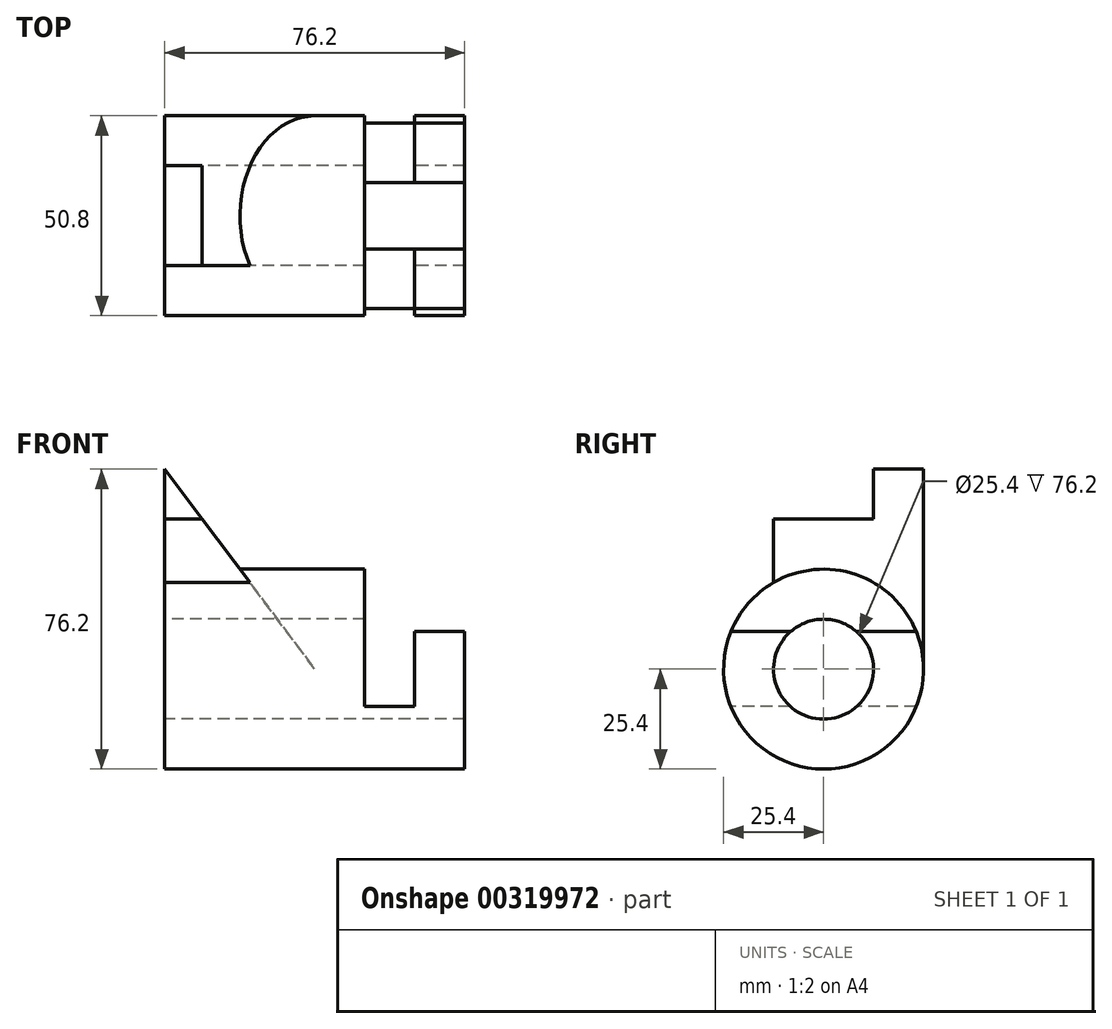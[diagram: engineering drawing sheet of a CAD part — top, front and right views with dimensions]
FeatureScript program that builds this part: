
annotation { "Feature Type Name" : "Feature", "Feature Type Description" : "" }
export const myFeature = defineFeature(function(context is Context, id is Id, definition is map)
    precondition{}
    {
        {
            var Q0;
            Q0=qCreatedBy(makeId("Front.planeOp"),FACE);
            var sketch = newSketch(context, id + "F0", { "sketchPlane" : qUnion([Q0])});
            skLineSegment(sketch, "E0", {"start": v(0, 0) * mm, "end": v(0, 25.4) * mm});
            skLineSegment(sketch, "E1", {"start": v(0, 25.4) * mm, "end": v(76.2, 25.4) * mm});
            skLineSegment(sketch, "E2", {"start": v(76.2, 25.4) * mm, "end": v(76.2, 0) * mm});
            skLineSegment(sketch, "E3", {"start": v(0, 0) * mm, "end": v(76.2, 0) * mm});
            skLineSegment(sketch, "E4", {"start": v(-18.96, 0) * mm, "end": v(97.99, 0) * mm, "construction": true});
            skSolve(sketch);
        }
        {
            var Q0;
            Q0=makeQuery(id+"F0.imprint","IMPRINT",FACE,{"disambiguationData":[TD([[makeQuery(id+"F0.imprint","IMPRINT",EDGE,{"derivedFrom":sQuery(id+"F0.wireOp",EDGE,"E0")}),-1.0]])]});
            var Q1;
            Q1=sQuery(id+"F0.wireOp",EDGE,"E4");
            revolve(context, id + "F1", {"entities" : qUnion([Q0]), "axis" : qUnion([Q1]), "revolveType" : RevolveType.FULL});
        }
        {
            var Q0;
            Q0=qCreatedBy(makeId("Front.planeOp"),FACE);
            var sketch = newSketch(context, id + "F2", { "sketchPlane" : qUnion([Q0])});
            skLineSegment(sketch, "E5", {"start": v(0, 25.4) * mm, "end": v(76.2, 25.4) * mm});
            skLineSegment(sketch, "E6", {"start": v(76.2, -25.4) * mm, "end": v(0, -25.4) * mm});
            skLineSegment(sketch, "E7.0", {"start": v(76.2, -25.4) * mm, "end": v(76.2, 25.4) * mm});
            skLineSegment(sketch, "E8", {"start": v(50.8, 25.4) * mm, "end": v(50.8, -9.53) * mm});
            skLineSegment(sketch, "E9", {"start": v(50.8, -9.53) * mm, "end": v(63.5, -9.53) * mm});
            skLineSegment(sketch, "E10", {"start": v(63.5, -9.53) * mm, "end": v(63.5, 9.52) * mm});
            skLineSegment(sketch, "E11", {"start": v(63.5, 9.52) * mm, "end": v(76.2, 9.52) * mm});
            skLineSegment(sketch, "E12", {"start": v(50.8, 25.4) * mm, "end": v(76.2, 25.4) * mm});
            skSolve(sketch);
        }
        {
            var Q0;
            Q0 = qSketchRegion(id + "F2", true);
            extrude(context, id + "F3", {"entities" : qUnion([Q0]), "operationType" : NewBodyOperationType.REMOVE, "endBound" : BoundingType.THROUGH_ALL, "oppositeDirection" : true, "depth" : 25.4 * mm, "hasSecondDirection" : true, "secondDirectionBound" : SecondDirectionBoundingType.THROUGH_ALL, "secondDirectionOppositeDirection" : false, "secondDirectionDepth" : 25.4 * mm});
        }
        {
            var Q0;
            Q0=qCreatedBy(makeId("Right.planeOp"),FACE);
            var sketch = newSketch(context, id + "F4", { "sketchPlane" : qUnion([Q0])});
            skArc(sketch, "E13.0", {"start": v(23.55, -9.53) * mm, "mid": v(0, 25.4) * mm, "end": v(-23.55, -9.53) * mm});
            skLineSegment(sketch, "E14", {"start": v(-12.7, 22) * mm, "end": v(-12.7, 38.1) * mm});
            skLineSegment(sketch, "E15", {"start": v(-12.7, 38.1) * mm, "end": v(12.7, 38.1) * mm});
            skLineSegment(sketch, "E16", {"start": v(12.7, 38.1) * mm, "end": v(12.7, 50.8) * mm});
            skLineSegment(sketch, "E17", {"start": v(12.7, 50.8) * mm, "end": v(25.4, 50.8) * mm});
            skLineSegment(sketch, "E18", {"start": v(25.4, 50.8) * mm, "end": v(25.4, 0) * mm});
            skSolve(sketch);
        }
        {
            var Q0;
            {var subQ0=sQuery(id+"F4.wireOp",EDGE,"E14");Q0=makeQuery(id+"F4.imprint","IMPRINT",FACE,{"disambiguationData":[TD([[makeQuery(id+"F4.imprint","IMPRINT",EDGE,{"derivedFrom":subQ0}),-1.0]])]});}
            extrude(context, id + "F5", {"entities" : qUnion([Q0]), "operationType" : NewBodyOperationType.ADD, "depth" : 38.1 * mm});
        }
        {
            var Q0;
            Q0=makeQuery(id+"F5.boolean.opBoolean","MERGE",FACE,{"derivedFrom":[makeQuery(id+"F1.opRevolve","SWEPT_FACE",FACE,{"disambiguationData":[OSD([sQuery(id+"F0.wireOp",EDGE,"E0")])]}),makeQuery(id+"F5.opExtrude","CAP_FACE",FACE,{"disambiguationData":[OSD([sQuery(id+"F4.wireOp",EDGE,"E13.0"),sQuery(id+"F4.wireOp",EDGE,"E14"),sQuery(id+"F4.wireOp",EDGE,"E15"),sQuery(id+"F4.wireOp",EDGE,"E16"),sQuery(id+"F4.wireOp",EDGE,"E17"),sQuery(id+"F4.wireOp",EDGE,"E18")])],"isStart":true})]});
            var sketch = newSketch(context, id + "F6", { "sketchPlane" : qUnion([Q0])});
            skCircle(sketch, "E19", {"center": v(0, 0) * mm, "radius": 12.7 * mm});
            skSolve(sketch);
        }
        {
            var Q0;
            Q0=makeQuery(id+"F6.imprint","IMPRINT",FACE,{"disambiguationData":[TD([[makeQuery(id+"F6.imprint","IMPRINT",EDGE,{"derivedFrom":sQuery(id+"F6.wireOp",EDGE,"E19")}),1.0]])]});
            extrude(context, id + "F7", {"entities" : qUnion([Q0]), "operationType" : NewBodyOperationType.REMOVE, "endBound" : BoundingType.THROUGH_ALL, "oppositeDirection" : true, "depth" : 25.4 * mm});
        }
        {
            var Q0;
            Q0=makeQuery(id+"F5.opExtrude","SWEPT_FACE",FACE,{"disambiguationData":[OSD([sQuery(id+"F4.wireOp",EDGE,"E14")])]});
            var sketch = newSketch(context, id + "F8", { "sketchPlane" : qUnion([Q0])});
            skLineSegment(sketch, "E20", {"start": v(38.1, 25.4) * mm, "end": v(50.8, 25.4) * mm});
            skLineSegment(sketch, "E21", {"start": v(76.2, -25.4) * mm, "end": v(0, -25.4) * mm});
            skLineSegment(sketch, "E22", {"start": v(38.1, 25.4) * mm, "end": v(38.1, 50.8) * mm});
            skPoint(sketch, "E22.endSnap0", {"position": v(38.1, 30.05) * mm});
            skLineSegment(sketch, "E23", {"start": v(38.1, 50.8) * mm, "end": v(0, 50.8) * mm});
            skLineSegment(sketch, "E24", {"start": v(0, 50.8) * mm, "end": v(0, 0) * mm});
            skLineSegment(sketch, "E25", {"start": v(0, 0) * mm, "end": v(38.1, 0) * mm});
            skLineSegment(sketch, "E26", {"start": v(38.1, 0) * mm, "end": v(38.1, 25.4) * mm});
            skLineSegment(sketch, "E27", {"start": v(38.1, 25.4) * mm, "end": v(0, 25.4) * mm});
            skLineSegment(sketch, "E28", {"start": v(50.8, 25.4) * mm, "end": v(50.8, 6.13) * mm});
            skLineSegment(sketch, "E29", {"start": v(0, 50.8) * mm, "end": v(38.1, 0) * mm});
            skSolve(sketch);
        }
        {
            var Q0;
            {var subQ3=sQuery(id+"F8.wireOp",EDGE,"E23");Q0=makeQuery(id+"F8.imprint","IMPRINT",FACE,{"disambiguationData":[TD([[makeQuery(id+"F8.imprint","IMPRINT",EDGE,{"derivedFrom":subQ3}),1.0]])]});}
            var Q1;
            {var subQ3=sQuery(id+"F8.wireOp",EDGE,"E27");var subQ5=sQuery(id+"F8.wireOp",EDGE,"E29");var subQ6=makeQuery(id+"F8.imprint","INTERSECT",VERTEX,{"derivedFrom":[subQ3,subQ5]});Q1=makeQuery(id+"F8.imprint","IMPRINT",FACE,{"disambiguationData":[TD([[makeQuery(id+"F8.imprint","IMPRINT",EDGE,{"disambiguationData":[TD([[subQ6,1.0]])],"derivedFrom":subQ3}),-1.0]])]});}
            extrude(context, id + "F9", {"entities" : qUnion([Q0, Q1]), "operationType" : NewBodyOperationType.REMOVE, "endBound" : BoundingType.THROUGH_ALL, "oppositeDirection" : true, "depth" : 25.4 * mm});
        }
        {
            var Q0;
            {var subQ0=sQuery(id+"F4.wireOp",EDGE,"E14");var subQ1=makeQuery(id+"F5.opExtrude","CAP_FACE",FACE,{"disambiguationData":[OSD([sQuery(id+"F4.wireOp",EDGE,"E13.0"),subQ0,sQuery(id+"F4.wireOp",EDGE,"E15"),sQuery(id+"F4.wireOp",EDGE,"E16"),sQuery(id+"F4.wireOp",EDGE,"E17"),sQuery(id+"F4.wireOp",EDGE,"E18")])],"isStart":false});Q0=makeQuery(id+"F9.boolean.opBoolean","SPLIT",FACE,{"disambiguationData":[TD([makeQuery(id+"F5.opExtrude","SWEPT_FACE",FACE,{"disambiguationData":[OSD([subQ0])]})])],"derivedFrom":subQ1});}
            var Q1;
            {var subQ0=sQuery(id+"F4.wireOp",EDGE,"E18");var subQ1=makeQuery(id+"F5.opExtrude","CAP_FACE",FACE,{"disambiguationData":[OSD([sQuery(id+"F4.wireOp",EDGE,"E13.0"),sQuery(id+"F4.wireOp",EDGE,"E14"),sQuery(id+"F4.wireOp",EDGE,"E15"),sQuery(id+"F4.wireOp",EDGE,"E16"),sQuery(id+"F4.wireOp",EDGE,"E17"),subQ0])],"isStart":false});Q1=makeQuery(id+"F9.boolean.opBoolean","SPLIT",FACE,{"disambiguationData":[TD([makeQuery(id+"F5.opExtrude","SWEPT_FACE",FACE,{"disambiguationData":[OSD([subQ0])]})])],"derivedFrom":subQ1});}
            var Q2;
            Q2=makeQuery(id+"F9.boolean.opBoolean","COPY",FACE,{"derivedFrom":makeQuery(id+"F9.opExtrude","SWEPT_FACE",FACE,{"disambiguationData":[OSD([sQuery(id+"F8.wireOp",EDGE,"E29")])]})});
            extrude(context, id + "F10", {"entities" : qUnion([Q0, Q1]), "operationType" : NewBodyOperationType.REMOVE, "endBound" : BoundingType.UP_TO_SURFACE, "oppositeDirection" : true, "endBoundEntityFace" : qUnion([Q2]), "depth" : 25.4 * mm});
        }
    });
